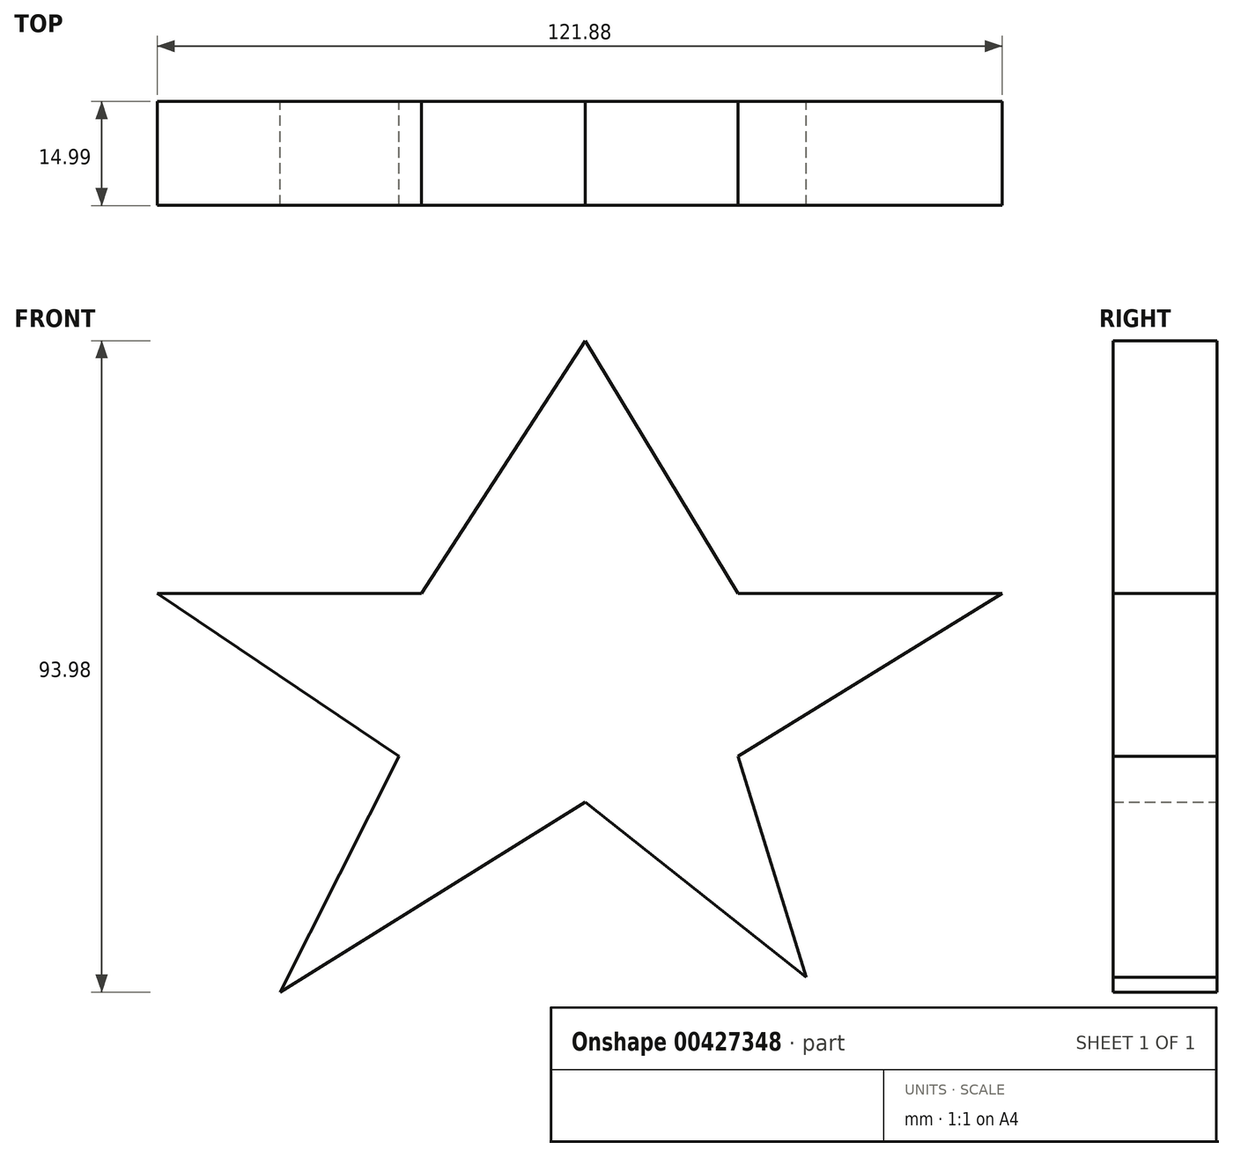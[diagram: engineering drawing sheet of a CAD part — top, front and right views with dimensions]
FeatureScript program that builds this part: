
annotation { "Feature Type Name" : "Feature", "Feature Type Description" : "" }
export const myFeature = defineFeature(function(context is Context, id is Id, definition is map)
    precondition{}
    {
        {
            var Q0;
            Q0=qCreatedBy(makeId("Front.planeOp"),FACE);
            var sketch = newSketch(context, id + "F0", { "sketchPlane" : qUnion([Q0])});
            skLineSegment(sketch, "E0", {"start": v(-23.68, 17.06) * mm, "end": v(-61.78, 17.06) * mm});
            skLineSegment(sketch, "E1", {"start": v(-61.78, 17.06) * mm, "end": v(-23.68, 17.06) * mm});
            skLineSegment(sketch, "E2", {"start": v(-61.78, 17.06) * mm, "end": v(-26.86, -6.42) * mm});
            skLineSegment(sketch, "E3", {"start": v(-26.86, -6.42) * mm, "end": v(-44.01, -40.45) * mm});
            skLineSegment(sketch, "E4", {"start": v(-44.01, -40.45) * mm, "end": v(0, -13.04) * mm});
            skLineSegment(sketch, "E5", {"start": v(0, -13.04) * mm, "end": v(31.83, -38.29) * mm});
            skLineSegment(sketch, "E6", {"start": v(31.83, -38.29) * mm, "end": v(22, -6.42) * mm});
            skLineSegment(sketch, "E7", {"start": v(22, -6.42) * mm, "end": v(60.1, 17.06) * mm});
            skLineSegment(sketch, "E8", {"start": v(60.1, 17.06) * mm, "end": v(22, 17.06) * mm});
            skLineSegment(sketch, "E9", {"start": v(-23.68, 17.06) * mm, "end": v(0, 53.53) * mm});
            skLineSegment(sketch, "E10", {"start": v(22, 17.06) * mm, "end": v(0, 53.53) * mm});
            skPoint(sketch, "E11.startSnap0", {"position": v(11, 35.3) * mm});
            skSolve(sketch);
        }
        {
            var Q0;
            Q0 = qSketchRegion(id + "F0", true);
            var Q1;
            Q1=makeQuery(id+"F0.imprint","IMPRINT",FACE,{"disambiguationData":[TD([[makeQuery(id+"F0.imprint","IMPRINT",EDGE,{"derivedFrom":sQuery(id+"F0.wireOp",EDGE,"E1")}),-1.0]])]});
            extrude(context, id + "F1", {"entities" : qUnion([Q0, Q1]), "depth" : 15 * mm});
        }
    });
